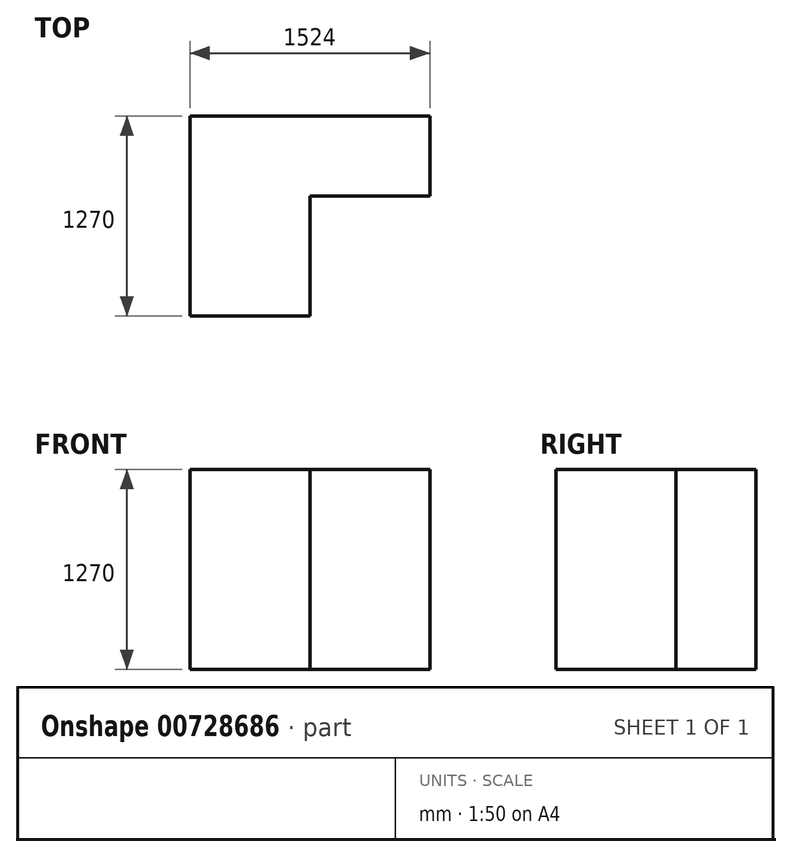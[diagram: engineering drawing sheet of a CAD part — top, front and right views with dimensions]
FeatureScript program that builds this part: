
annotation { "Feature Type Name" : "Feature", "Feature Type Description" : "" }
export const myFeature = defineFeature(function(context is Context, id is Id, definition is map)
    precondition{}
    {
        {
            var Q0;
            Q0=qCreatedBy(makeId("Front.planeOp"),FACE);
            var sketch = newSketch(context, id + "F0", { "sketchPlane" : qUnion([Q0])});
            skLineSegment(sketch, "E0", {"start": v(0, 0) * mm, "end": v(1524, 0) * mm});
            skLineSegment(sketch, "E1", {"start": v(1524, 0) * mm, "end": v(1524, 1270) * mm});
            skLineSegment(sketch, "E2", {"start": v(1524, 1270) * mm, "end": v(0, 1270) * mm});
            skLineSegment(sketch, "E3", {"start": v(0, 0) * mm, "end": v(0, 1270) * mm});
            skSolve(sketch);
        }
        {
            var Q0;
            Q0 = qSketchRegion(id + "F0", true);
            extrude(context, id + "F1", {"entities" : qUnion([Q0]), "depth" : 1270 * mm, "offsetDistance" : 25.4 * mm});
        }
        {
            var Q0;
            Q0=makeQuery(id+"F1.opExtrude","SWEPT_FACE",FACE,{"disambiguationData":[OSD([sQuery(id+"F0.wireOp",EDGE,"E2")])]});
            var sketch = newSketch(context, id + "F2", { "sketchPlane" : qUnion([Q0])});
            skLineSegment(sketch, "E4", {"start": v(762, -1270) * mm, "end": v(762, -508) * mm});
            skLineSegment(sketch, "E5", {"start": v(762, -508) * mm, "end": v(1524, -508) * mm});
            skLineSegment(sketch, "E6", {"start": v(1524, -508) * mm, "end": v(1524, -1270) * mm});
            skLineSegment(sketch, "E7", {"start": v(1524, -1270) * mm, "end": v(762, -1270) * mm});
            skSolve(sketch);
        }
        {
            var Q0;
            Q0=makeQuery(id+"F2.imprint","IMPRINT",FACE,{"disambiguationData":[TD([[makeQuery(id+"F2.imprint","IMPRINT",EDGE,{"derivedFrom":sQuery(id+"F2.wireOp",EDGE,"E4")}),-1.0]])]});
            extrude(context, id + "F3", {"entities" : qUnion([Q0]), "operationType" : NewBodyOperationType.REMOVE, "endBound" : BoundingType.THROUGH_ALL, "oppositeDirection" : true, "depth" : 25.4 * mm, "offsetDistance" : 25.4 * mm});
        }
    });
